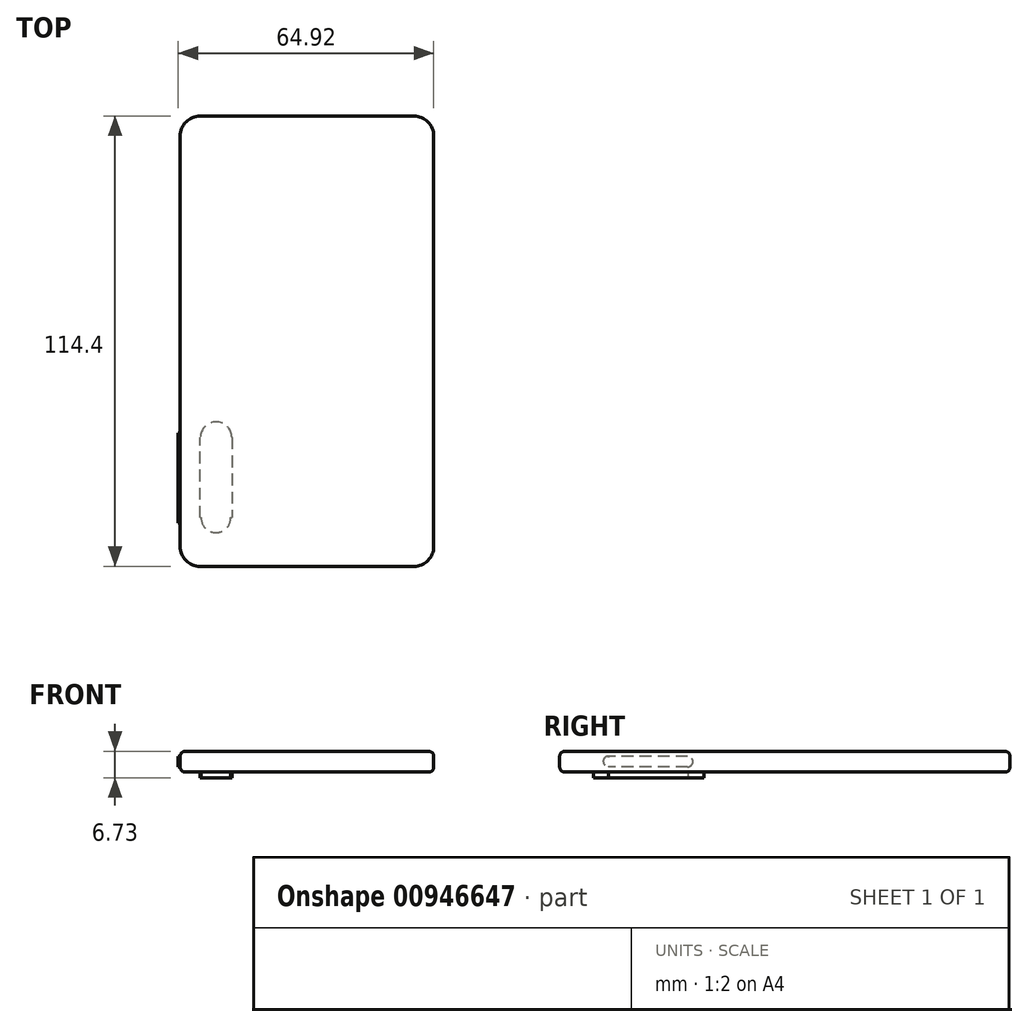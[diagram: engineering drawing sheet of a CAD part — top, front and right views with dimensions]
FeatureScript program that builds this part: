
annotation { "Feature Type Name" : "Feature", "Feature Type Description" : "" }
export const myFeature = defineFeature(function(context is Context, id is Id, definition is map)
    precondition{}
    {
        {
            var Q0;
            Q0=qCreatedBy(makeId("Top.planeOp"),FACE);
            var sketch = newSketch(context, id + "F0", { "sketchPlane" : qUnion([Q0])});
            skLineSegment(sketch, "E0.bottom", {"start": v(-34.46, 49.26) * mm, "end": v(29.95, 49.26) * mm});
            skLineSegment(sketch, "E0.top", {"start": v(-34.46, -65.14) * mm, "end": v(29.95, -65.14) * mm});
            skLineSegment(sketch, "E0.left", {"start": v(-34.46, 49.26) * mm, "end": v(-34.46, -65.14) * mm});
            skLineSegment(sketch, "E0.right", {"start": v(29.95, 49.26) * mm, "end": v(29.95, -65.14) * mm});
            skSolve(sketch);
        }
        {
            var Q0;
            Q0=makeQuery(id+"F0.imprint","IMPRINT",FACE,{"disambiguationData":[TD([[makeQuery(id+"F0.imprint","IMPRINT",EDGE,{"derivedFrom":sQuery(id+"F0.wireOp",EDGE,"E0.bottom")}),-1.0]])]});
            extrude(context, id + "F1", {"entities" : qUnion([Q0]), "depth" : 5.28 * mm, "offsetDistance" : 25.4 * mm});
        }
        {
            var Q0;
            Q0=makeQuery(id+"F1.opExtrude","CAP_FACE",FACE,{"disambiguationData":[OSD([sQuery(id+"F0.wireOp",EDGE,"E0.bottom"),sQuery(id+"F0.wireOp",EDGE,"E0.top"),sQuery(id+"F0.wireOp",EDGE,"E0.left"),sQuery(id+"F0.wireOp",EDGE,"E0.right")])],"isStart":false});
            fillet(context, id + "F2", {"entities" : qUnion([Q0]), "radius" : 1.27 * mm, "tangentPropagation" : true, "allowEdgeOverflow" : false});
        }
        {
            var Q0;
            Q0=makeQuery(id+"F1.opExtrude","CAP_FACE",FACE,{"disambiguationData":[OSD([sQuery(id+"F0.wireOp",EDGE,"E0.bottom"),sQuery(id+"F0.wireOp",EDGE,"E0.top"),sQuery(id+"F0.wireOp",EDGE,"E0.left"),sQuery(id+"F0.wireOp",EDGE,"E0.right")])],"isStart":true});
            fillet(context, id + "F3", {"entities" : qUnion([Q0]), "radius" : 1.27 * mm, "tangentPropagation" : true, "allowEdgeOverflow" : false});
        }
        {
            var Q0;
            Q0=makeQuery(id+"F1.opExtrude","SWEPT_EDGE",EDGE,{"disambiguationData":[OSD([sQuery(id+"F0.wireOp",EDGE,"E0.bottom"),sQuery(id+"F0.wireOp",EDGE,"E0.left")])]});
            fillet(context, id + "F4", {"entities" : qUnion([Q0]), "radius" : 5.08 * mm, "tangentPropagation" : true, "allowEdgeOverflow" : false});
        }
        {
            var Q0;
            Q0=makeQuery(id+"F1.opExtrude","SWEPT_EDGE",EDGE,{"disambiguationData":[OSD([sQuery(id+"F0.wireOp",EDGE,"E0.bottom"),sQuery(id+"F0.wireOp",EDGE,"E0.right")])]});
            fillet(context, id + "F5", {"entities" : qUnion([Q0]), "radius" : 5.08 * mm, "tangentPropagation" : true, "allowEdgeOverflow" : false});
        }
        {
            var Q0;
            Q0=makeQuery(id+"F1.opExtrude","SWEPT_EDGE",EDGE,{"disambiguationData":[OSD([sQuery(id+"F0.wireOp",EDGE,"E0.top"),sQuery(id+"F0.wireOp",EDGE,"E0.right")])]});
            fillet(context, id + "F6", {"entities" : qUnion([Q0]), "radius" : 5.08 * mm, "tangentPropagation" : true, "allowEdgeOverflow" : false});
        }
        {
            var Q0;
            Q0=makeQuery(id+"F1.opExtrude","SWEPT_EDGE",EDGE,{"disambiguationData":[OSD([sQuery(id+"F0.wireOp",EDGE,"E0.top"),sQuery(id+"F0.wireOp",EDGE,"E0.left")])]});
            fillet(context, id + "F7", {"entities" : qUnion([Q0]), "radius" : 5.08 * mm, "tangentPropagation" : true, "allowEdgeOverflow" : false});
        }
        {
            var Q0;
            Q0=makeQuery(id+"F1.opExtrude","CAP_FACE",FACE,{"disambiguationData":[OSD([sQuery(id+"F0.wireOp",EDGE,"E0.bottom"),sQuery(id+"F0.wireOp",EDGE,"E0.top"),sQuery(id+"F0.wireOp",EDGE,"E0.left"),sQuery(id+"F0.wireOp",EDGE,"E0.right")])],"isStart":true});
            var sketch = newSketch(context, id + "F8", { "sketchPlane" : qUnion([Q0])});
            skLineSegment(sketch, "E1.bottom", {"start": v(-29.38, 52.78) * mm, "end": v(-21.34, 52.78) * mm});
            skLineSegment(sketch, "E1.top", {"start": v(-29.38, 32.39) * mm, "end": v(-21.34, 32.39) * mm});
            skLineSegment(sketch, "E1.left", {"start": v(-29.38, 52.78) * mm, "end": v(-29.38, 32.39) * mm});
            skLineSegment(sketch, "E1.right", {"start": v(-21.34, 52.78) * mm, "end": v(-21.34, 32.39) * mm});
            skSolve(sketch);
        }
        {
            var Q0;
            Q0=makeQuery(id+"F8.imprint","IMPRINT",FACE,{"disambiguationData":[TD([[makeQuery(id+"F8.imprint","IMPRINT",EDGE,{"derivedFrom":sQuery(id+"F8.wireOp",EDGE,"E1.bottom")}),-1.0]])]});
            var sketch = newSketch(context, id + "F9", { "sketchPlane" : qUnion([Q0])});
            skCircle(sketch, "E2", {"center": v(-25.38, 52.83) * mm, "radius": 3.76 * mm});
            skSolve(sketch);
        }
        {
            var Q0;
            Q0=makeQuery(id+"F9.imprint","IMPRINT",FACE,{"disambiguationData":[TD([[makeQuery(id+"F9.imprint","IMPRINT",EDGE,{"derivedFrom":makeQuery(id+"F8.imprint","IMPRINT",EDGE,{"derivedFrom":sQuery(id+"F8.wireOp",EDGE,"E1.top")})}),1.0]])]});
            var sketch = newSketch(context, id + "F10", { "sketchPlane" : qUnion([Q0])});
            skCircle(sketch, "E3", {"center": v(-25.33, 32.42) * mm, "radius": 4 * mm});
            skSolve(sketch);
        }
        {
            var Q0;
            Q0=makeQuery(id+"F9.imprint","IMPRINT",FACE,{"disambiguationData":[TD([[makeQuery(id+"F9.imprint","IMPRINT",EDGE,{"derivedFrom":makeQuery(id+"F8.imprint","IMPRINT",EDGE,{"derivedFrom":sQuery(id+"F8.wireOp",EDGE,"E1.top")})}),1.0]])]});
            var Q1;
            Q1 = qSketchRegion(id + "F10", true);
            var Q2;
            Q2 = qSketchRegion(id + "F8", true);
            var Q3;
            Q3 = qSketchRegion(id + "F9", true);
            extrude(context, id + "F11", {"entities" : qUnion([Q0, Q1, Q2, Q3]), "operationType" : NewBodyOperationType.ADD, "depth" : 1.45 * mm, "offsetDistance" : 25.4 * mm});
        }
        {
            var Q0;
            Q0=makeQuery(id+"F1.opExtrude","SWEPT_FACE",FACE,{"disambiguationData":[OSD([sQuery(id+"F0.wireOp",EDGE,"E0.right")])]});
            var sketch = newSketch(context, id + "F12", { "sketchPlane" : qUnion([Q0])});
            skLineSegment(sketch, "E4.bottom", {"start": v(-52.88, 4) * mm, "end": v(-39.01, 4) * mm});
            skLineSegment(sketch, "E4.top", {"start": v(-52.88, 1.27) * mm, "end": v(-39.01, 1.27) * mm});
            skLineSegment(sketch, "E4.left", {"start": v(-52.88, 4) * mm, "end": v(-52.88, 1.27) * mm});
            skLineSegment(sketch, "E4.right", {"start": v(-39.01, 4) * mm, "end": v(-39.01, 1.27) * mm});
            skSolve(sketch);
        }
        {
            var Q0;
            Q0=makeQuery(id+"F12.imprint","IMPRINT",FACE,{"disambiguationData":[TD([[makeQuery(id+"F12.imprint","IMPRINT",EDGE,{"derivedFrom":sQuery(id+"F12.wireOp",EDGE,"E4.bottom")}),1.0]])]});
            var sketch = newSketch(context, id + "F13", { "sketchPlane" : qUnion([Q0])});
            skCircle(sketch, "E5", {"center": v(-52.82, 2.72) * mm, "radius": 1.16 * mm});
            skSolve(sketch);
        }
        {
            var Q0;
            Q0=makeQuery(id+"F1.opExtrude","SWEPT_FACE",FACE,{"disambiguationData":[OSD([sQuery(id+"F0.wireOp",EDGE,"E0.left")])]});
            var sketch = newSketch(context, id + "F14", { "sketchPlane" : qUnion([Q0])});
            skLineSegment(sketch, "E6.bottom", {"start": v(32.63, 4) * mm, "end": v(52.74, 4) * mm});
            skLineSegment(sketch, "E6.top", {"start": v(32.63, 1.27) * mm, "end": v(52.74, 1.27) * mm});
            skLineSegment(sketch, "E6.left", {"start": v(32.63, 4) * mm, "end": v(32.63, 1.27) * mm});
            skLineSegment(sketch, "E6.right", {"start": v(52.74, 4) * mm, "end": v(52.74, 1.27) * mm});
            skSolve(sketch);
        }
        {
            var Q0;
            Q0=makeQuery(id+"F14.imprint","IMPRINT",FACE,{"disambiguationData":[TD([[makeQuery(id+"F14.imprint","IMPRINT",EDGE,{"derivedFrom":sQuery(id+"F14.wireOp",EDGE,"E6.bottom")}),1.0]])]});
            var sketch = newSketch(context, id + "F15", { "sketchPlane" : qUnion([Q0])});
            skCircle(sketch, "E7", {"center": v(52.77, 2.71) * mm, "radius": 1.32 * mm});
            skSolve(sketch);
        }
        {
            var Q0;
            Q0=makeQuery(id+"F14.imprint","IMPRINT",FACE,{"disambiguationData":[TD([[makeQuery(id+"F14.imprint","IMPRINT",EDGE,{"derivedFrom":sQuery(id+"F14.wireOp",EDGE,"E6.bottom")}),1.0]])]});
            var sketch = newSketch(context, id + "F16", { "sketchPlane" : qUnion([Q0])});
            skCircle(sketch, "E8", {"center": v(32.64, 2.65) * mm, "radius": 1.33 * mm});
            skSolve(sketch);
        }
        {
            var Q0;
            Q0=makeQuery(id+"F14.imprint","IMPRINT",FACE,{"disambiguationData":[TD([[makeQuery(id+"F14.imprint","IMPRINT",EDGE,{"derivedFrom":sQuery(id+"F14.wireOp",EDGE,"E6.bottom")}),1.0]])]});
            var Q1;
            Q1 = qSketchRegion(id + "F15", true);
            var Q2;
            Q2 = qSketchRegion(id + "F16", true);
            extrude(context, id + "F17", {"entities" : qUnion([Q0, Q1, Q2]), "operationType" : NewBodyOperationType.ADD, "depth" : 0.5 * mm, "offsetDistance" : 25.4 * mm});
        }
    });
